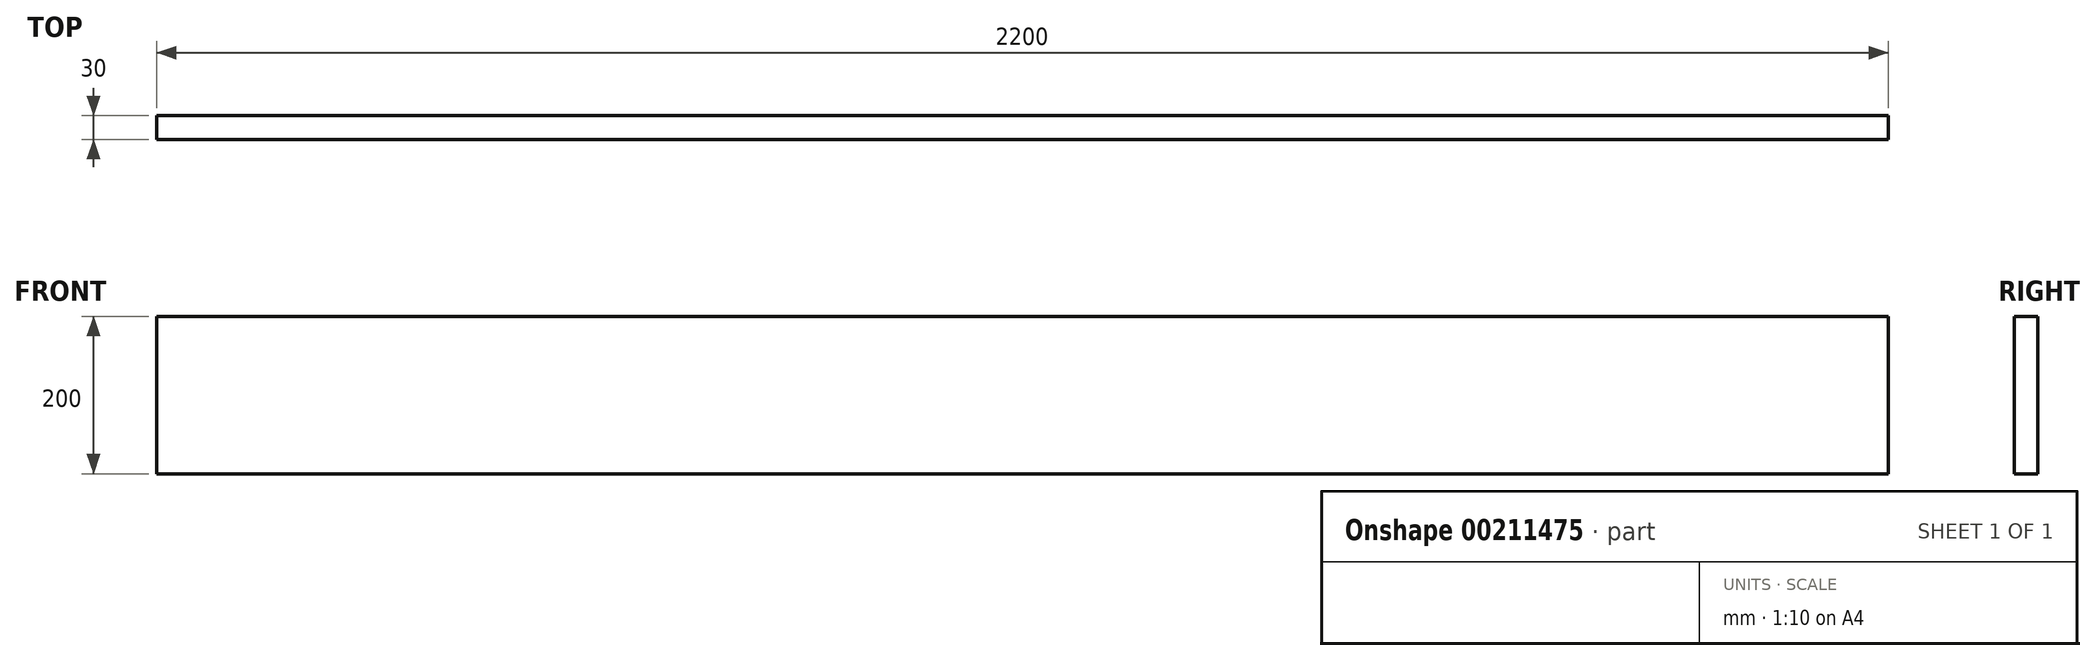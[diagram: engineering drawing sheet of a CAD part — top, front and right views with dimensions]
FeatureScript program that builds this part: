
annotation { "Feature Type Name" : "Feature", "Feature Type Description" : "" }
export const myFeature = defineFeature(function(context is Context, id is Id, definition is map)
    precondition{}
    {
        {
            var Q0;
            Q0=qCreatedBy(makeId("Front.planeOp"),FACE);
            var sketch = newSketch(context, id + "F0", { "sketchPlane" : qUnion([Q0])});
            skLineSegment(sketch, "E0.bottom", {"start": v(1100, 100) * mm, "end": v(-1100, 100) * mm});
            skLineSegment(sketch, "E0.top", {"start": v(1100, -100) * mm, "end": v(-1100, -100) * mm});
            skLineSegment(sketch, "E0.left", {"start": v(1100, 100) * mm, "end": v(1100, -100) * mm});
            skLineSegment(sketch, "E0.right", {"start": v(-1100, 100) * mm, "end": v(-1100, -100) * mm});
            skPoint(sketch, "E0.middle", {"position": v(0, 0) * mm});
            skSolve(sketch);
        }
        {
            var Q0;
            Q0=qSketchRegion(id+"F0",true);
            extrude(context, id + "F1", {"entities" : qUnion([Q0]), "depth" : 30 * mm});
        }
    });
